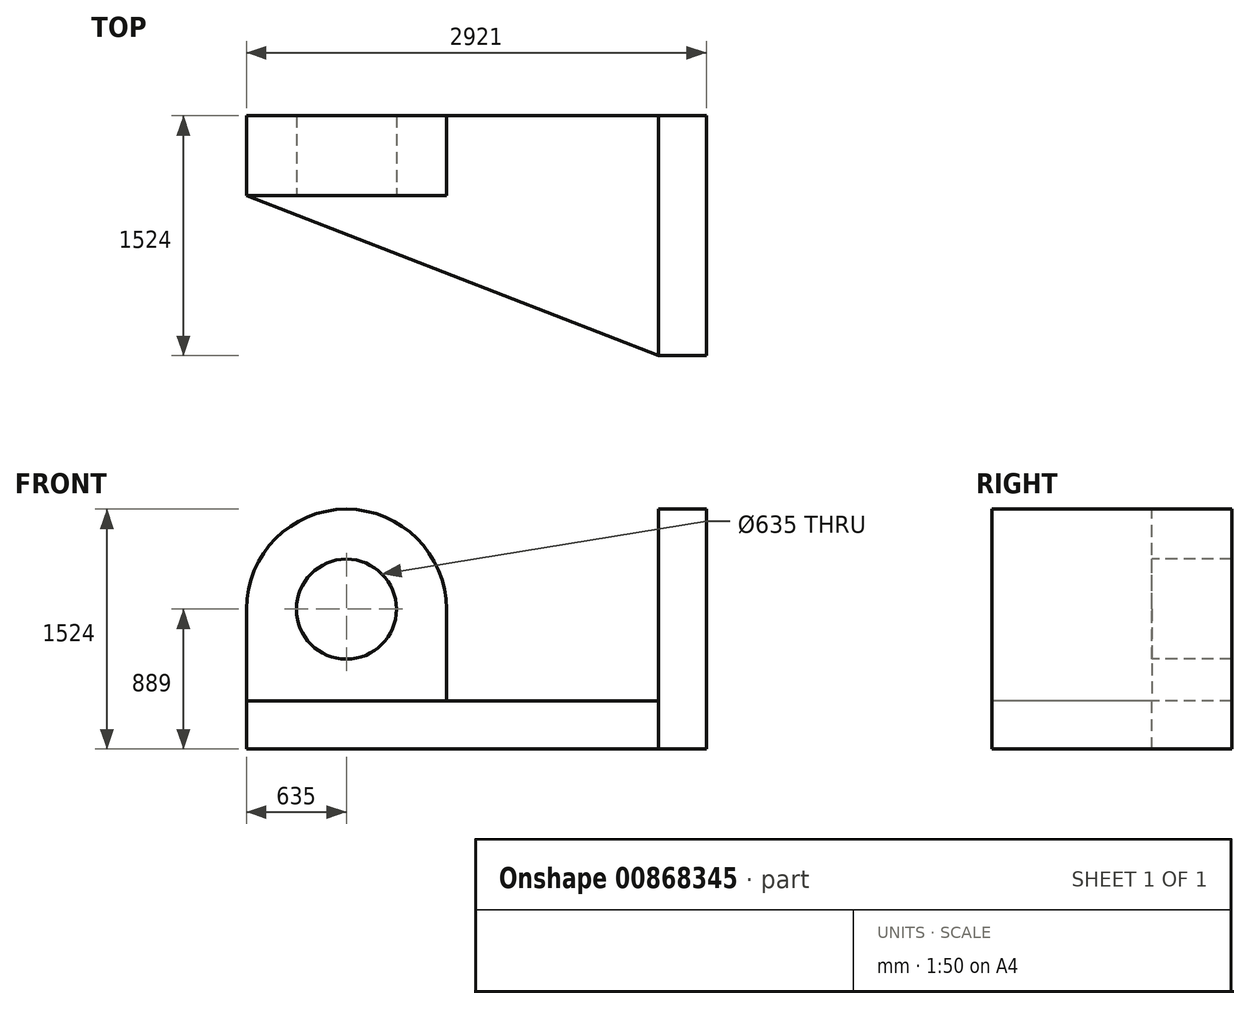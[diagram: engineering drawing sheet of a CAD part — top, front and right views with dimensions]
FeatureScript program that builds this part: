
annotation { "Feature Type Name" : "Feature", "Feature Type Description" : "" }
export const myFeature = defineFeature(function(context is Context, id is Id, definition is map)
    precondition{}
    {
        {
            var Q0;
            Q0=qCreatedBy(makeId("Front.planeOp"),FACE);
            var sketch = newSketch(context, id + "F0", { "sketchPlane" : qUnion([Q0])});
            skLineSegment(sketch, "E0.bottom", {"start": v(0, 0) * mm, "end": v(-2921, 0) * mm});
            skLineSegment(sketch, "E0.top", {"start": v(0, 1524) * mm, "end": v(-2921, 1524) * mm});
            skLineSegment(sketch, "E0.left", {"start": v(0, 0) * mm, "end": v(0, 1524) * mm});
            skLineSegment(sketch, "E0.right", {"start": v(-2921, 0) * mm, "end": v(-2921, 1524) * mm});
            skSolve(sketch);
        }
        {
            var Q0;
            Q0=makeQuery(id+"F0.imprint","IMPRINT",FACE,{"disambiguationData":[TD([[makeQuery(id+"F0.imprint","IMPRINT",EDGE,{"derivedFrom":sQuery(id+"F0.wireOp",EDGE,"E0.bottom")}),-1.0]])]});
            extrude(context, id + "F1", {"entities" : qUnion([Q0]), "depth" : 1524 * mm, "offsetDistance" : 25.4 * mm});
        }
        {
            var Q0;
            Q0=makeQuery(id+"F1.opExtrude","CAP_FACE",FACE,{"disambiguationData":[OSD([sQuery(id+"F0.wireOp",EDGE,"E0.bottom"),sQuery(id+"F0.wireOp",EDGE,"E0.top"),sQuery(id+"F0.wireOp",EDGE,"E0.left"),sQuery(id+"F0.wireOp",EDGE,"E0.right")])],"isStart":false});
            var sketch = newSketch(context, id + "F2", { "sketchPlane" : qUnion([Q0])});
            skLineSegment(sketch, "E1", {"start": v(-2921, 0) * mm, "end": v(-2921, 304.8) * mm});
            skLineSegment(sketch, "E2", {"start": v(-2921, 304.8) * mm, "end": v(-304.8, 304.8) * mm});
            skLineSegment(sketch, "E3", {"start": v(-304.8, 304.8) * mm, "end": v(-304.8, 1524) * mm});
            skSolve(sketch);
        }
        {
            var Q0;
            {var subQ0=sQuery(id+"F2.wireOp",EDGE,"E2");Q0=makeQuery(id+"F2.imprint","IMPRINT",FACE,{"disambiguationData":[TD([[makeQuery(id+"F2.imprint","IMPRINT",EDGE,{"derivedFrom":subQ0}),1.0]])]});}
            extrude(context, id + "F3", {"entities" : qUnion([Q0]), "operationType" : NewBodyOperationType.REMOVE, "oppositeDirection" : true, "depth" : 1016 * mm, "offsetDistance" : 25.4 * mm});
        }
        {
            var Q0;
            Q0=makeQuery(id+"F1.opExtrude","SWEPT_FACE",FACE,{"disambiguationData":[OSD([sQuery(id+"F0.wireOp",EDGE,"E0.top")])]});
            var sketch = newSketch(context, id + "F4", { "sketchPlane" : qUnion([Q0])});
            skLineSegment(sketch, "E4", {"start": v(-304.8, -508) * mm, "end": v(-304.8, 0) * mm});
            skLineSegment(sketch, "E5", {"start": v(-304.8, 0) * mm, "end": v(-1651, 0) * mm});
            skLineSegment(sketch, "E6", {"start": v(-1651, 0) * mm, "end": v(-1651, -508) * mm});
            skSolve(sketch);
        }
        {
            var Q0;
            {var subQ0=sQuery(id+"F4.wireOp",EDGE,"E4");Q0=makeQuery(id+"F4.imprint","IMPRINT",FACE,{"disambiguationData":[TD([[makeQuery(id+"F4.imprint","IMPRINT",EDGE,{"derivedFrom":subQ0}),1.0]])]});}
            extrude(context, id + "F5", {"entities" : qUnion([Q0]), "operationType" : NewBodyOperationType.REMOVE, "oppositeDirection" : true, "depth" : 1219.2 * mm, "offsetDistance" : 25.4 * mm});
        }
        {
            var Q0;
            Q0=makeQuery(id+"F5.boolean.opBoolean","MERGE",FACE,{"derivedFrom":[makeQuery(id+"F3.boolean.opBoolean","COPY",FACE,{"derivedFrom":makeQuery(id+"F3.opExtrude","SWEPT_FACE",FACE,{"disambiguationData":[OSD([sQuery(id+"F2.wireOp",EDGE,"E2")])]})}),makeQuery(id+"F5.opExtrude","CAP_FACE",FACE,{"disambiguationData":[OSD([sQuery(id+"F0.wireOp",EDGE,"E0.top"),sQuery(id+"F4.wireOp",EDGE,"E4"),sQuery(id+"F4.wireOp",EDGE,"E5"),sQuery(id+"F4.wireOp",EDGE,"E6")])],"isStart":false})]});
            var sketch = newSketch(context, id + "F6", { "sketchPlane" : qUnion([Q0])});
            skLineSegment(sketch, "E7", {"start": v(-2921, -508) * mm, "end": v(-304.8, -1524) * mm});
            skSolve(sketch);
        }
        {
            var Q0;
            Q0=makeQuery(id+"F6.imprint","IMPRINT",FACE,{"disambiguationData":[TD([[makeQuery(id+"F6.imprint","IMPRINT",EDGE,{"derivedFrom":sQuery(id+"F6.wireOp",EDGE,"E7")}),-1.0]])]});
            extrude(context, id + "F7", {"entities" : qUnion([Q0]), "operationType" : NewBodyOperationType.REMOVE, "oppositeDirection" : true, "depth" : 1270 * mm, "offsetDistance" : 25.4 * mm});
        }
        {
            var Q0;
            {var subQ0=sQuery(id+"F0.wireOp",EDGE,"E0.right");var subQ1=sQuery(id+"F0.wireOp",EDGE,"E0.top");Q0=makeQuery(id+"F5.boolean.opBoolean","SPLIT",FACE,{"disambiguationData":[TD([makeQuery(id+"F1.opExtrude","SWEPT_FACE",FACE,{"disambiguationData":[OSD([subQ0])]})])],"derivedFrom":makeQuery(id+"F1.opExtrude","SWEPT_FACE",FACE,{"disambiguationData":[OSD([subQ1])]})});}
            extrude(context, id + "F8", {"entities" : qUnion([Q0]), "operationType" : NewBodyOperationType.REMOVE, "oppositeDirection" : true, "depth" : 1219.2 * mm, "offsetDistance" : 25.4 * mm});
        }
        {
            var Q0;
            {var subQ0=sQuery(id+"F0.wireOp",EDGE,"E0.top");Q0=makeQuery(id+"F8.boolean.opBoolean","MERGE",FACE,{"derivedFrom":[makeQuery(id+"F5.boolean.opBoolean","MERGE",FACE,{"derivedFrom":[makeQuery(id+"F3.boolean.opBoolean","COPY",FACE,{"derivedFrom":makeQuery(id+"F3.opExtrude","SWEPT_FACE",FACE,{"disambiguationData":[OSD([sQuery(id+"F2.wireOp",EDGE,"E2")])]})}),makeQuery(id+"F5.opExtrude","CAP_FACE",FACE,{"disambiguationData":[OSD([subQ0,sQuery(id+"F4.wireOp",EDGE,"E4"),sQuery(id+"F4.wireOp",EDGE,"E5"),sQuery(id+"F4.wireOp",EDGE,"E6")])],"isStart":false})]}),makeQuery(id+"F8.opExtrude","CAP_FACE",FACE,{"disambiguationData":[OSD([subQ0])],"isStart":false})]});}
            var sketch = newSketch(context, id + "F9", { "sketchPlane" : qUnion([Q0])});
            skLineSegment(sketch, "E8.bottom", {"start": v(-2921, 0) * mm, "end": v(-1651, 0) * mm});
            skLineSegment(sketch, "E8.top", {"start": v(-2921, -508) * mm, "end": v(-1651, -508) * mm});
            skLineSegment(sketch, "E8.left", {"start": v(-2921, 0) * mm, "end": v(-2921, -508) * mm});
            skLineSegment(sketch, "E8.right", {"start": v(-1651, 0) * mm, "end": v(-1651, -508) * mm});
            skSolve(sketch);
        }
        {
            var Q0;
            Q0=makeQuery(id+"F9.imprint","IMPRINT",FACE,{"disambiguationData":[TD([[makeQuery(id+"F9.imprint","IMPRINT",EDGE,{"derivedFrom":sQuery(id+"F9.wireOp",EDGE,"E8.bottom")}),1.0]])]});
            extrude(context, id + "F10", {"entities" : qUnion([Q0]), "operationType" : NewBodyOperationType.ADD, "depth" : 584.2 * mm, "offsetDistance" : 25.4 * mm});
        }
        {
            var Q0;
            Q0=makeQuery(id+"F10.opExtrude","SWEPT_FACE",FACE,{"disambiguationData":[OSD([sQuery(id+"F9.wireOp",EDGE,"E8.top")])]});
            var sketch = newSketch(context, id + "F11", { "sketchPlane" : qUnion([Q0])});
            skCircle(sketch, "E9", {"center": v(-2286, 889) * mm, "radius": 635 * mm});
            skSolve(sketch);
        }
        {
            var Q0;
            {var subQ1=sQuery(id+"F9.wireOp",EDGE,"E8.top");var subQ2=makeQuery(id+"F10.opExtrude","CAP_EDGE",EDGE,{"disambiguationData":[OSD([subQ1])],"isStart":false});Q0=makeQuery(id+"F11.imprint","IMPRINT",FACE,{"disambiguationData":[TD([[makeQuery(id+"F11.imprint","IMPRINT",EDGE,{"derivedFrom":subQ2}),1.0]])]});}
            extrude(context, id + "F12", {"entities" : qUnion([Q0]), "operationType" : NewBodyOperationType.ADD, "oppositeDirection" : true, "depth" : 508 * mm, "offsetDistance" : 25.4 * mm});
        }
        {
            var Q0;
            {var subQ0=sQuery(id+"F9.wireOp",EDGE,"E8.top");Q0=makeQuery(id+"F12.boolean.opBoolean","MERGE",FACE,{"derivedFrom":[makeQuery(id+"F10.opExtrude","SWEPT_FACE",FACE,{"disambiguationData":[OSD([subQ0])]}),makeQuery(id+"F12.opExtrude","CAP_FACE",FACE,{"disambiguationData":[OSD([subQ0,sQuery(id+"F11.wireOp",EDGE,"E9")])],"isStart":true})]});}
            var sketch = newSketch(context, id + "F13", { "sketchPlane" : qUnion([Q0])});
            skCircle(sketch, "E10", {"center": v(-2286, 889) * mm, "radius": 317.5 * mm});
            skSolve(sketch);
        }
        {
            var Q0;
            Q0=makeQuery(id+"F13.imprint","IMPRINT",FACE,{"disambiguationData":[TD([[makeQuery(id+"F13.imprint","IMPRINT",EDGE,{"derivedFrom":sQuery(id+"F13.wireOp",EDGE,"E10")}),1.0]])]});
            extrude(context, id + "F14", {"entities" : qUnion([Q0]), "operationType" : NewBodyOperationType.REMOVE, "oppositeDirection" : true, "depth" : 1270 * mm, "offsetDistance" : 25.4 * mm});
        }
    });
